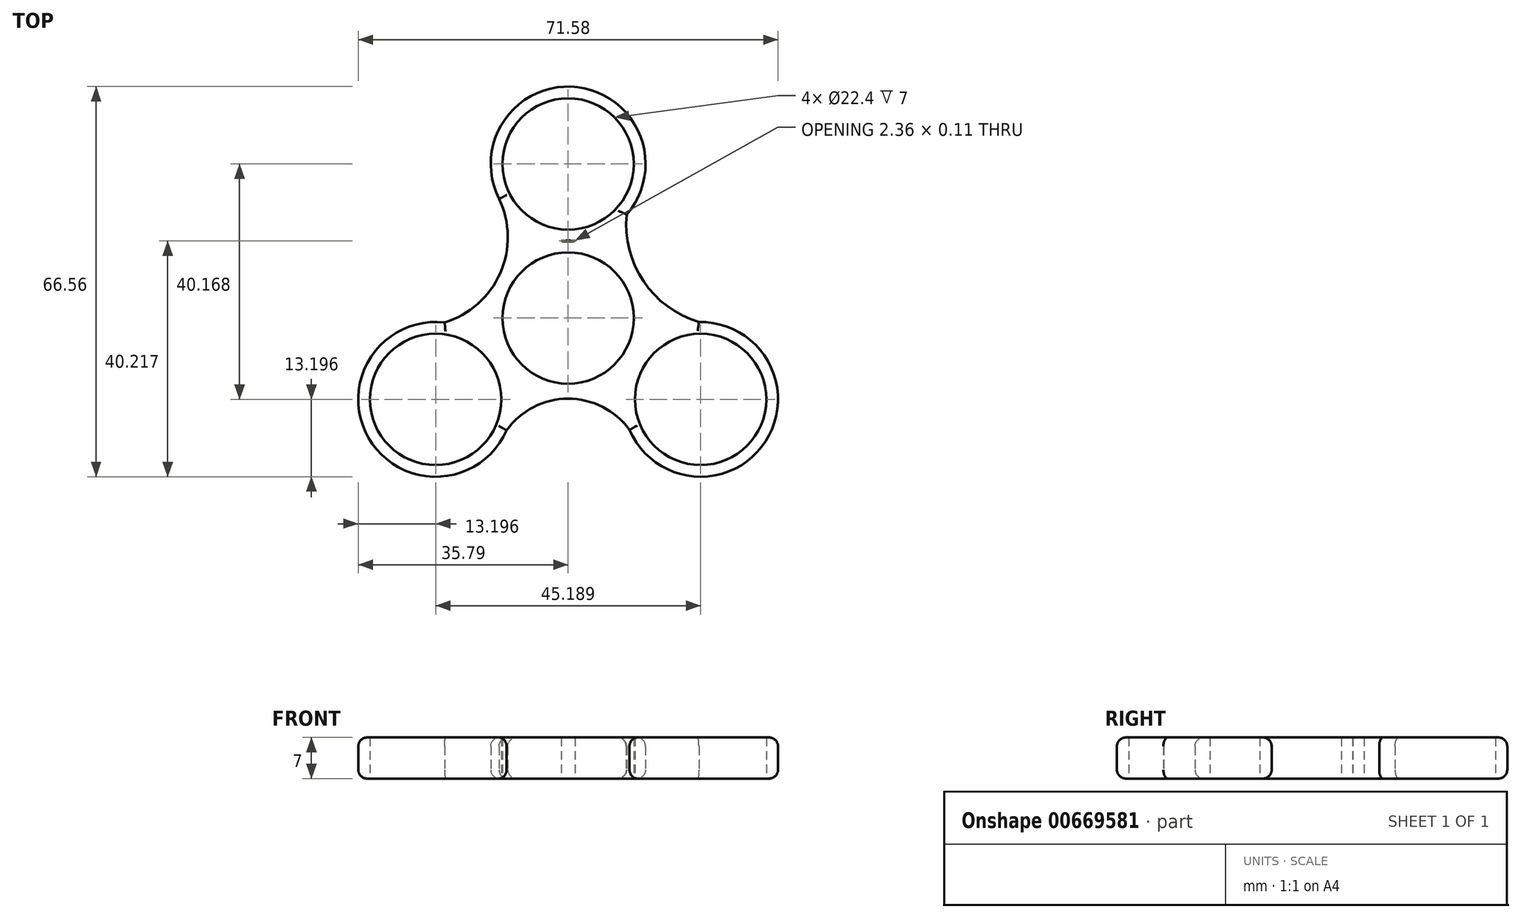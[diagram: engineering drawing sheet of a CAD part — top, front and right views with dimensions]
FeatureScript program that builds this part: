
annotation { "Feature Type Name" : "Feature", "Feature Type Description" : "" }
export const myFeature = defineFeature(function(context is Context, id is Id, definition is map)
    precondition{}
    {
        {
            var Q0;
            Q0=qCreatedBy(makeId("Top.planeOp"),FACE);
            var sketch = newSketch(context, id + "F0", { "sketchPlane" : qUnion([Q0])});
            skCircle(sketch, "E0", {"center": v(0, 0) * mm, "radius": 11.2 * mm});
            skArc(sketch, "E1", {"start": v(1.18, 13.15) * mm, "mid": v(0, 13.2) * mm, "end": v(-1.18, 13.15) * mm});
            skCircle(sketch, "E2", {"center": v(0, 26.3) * mm, "radius": 11.2 * mm});
            skArc(sketch, "E3", {"start": v(9.98, 17.66) * mm, "mid": v(1.62, 39.4) * mm, "end": v(-11.78, 20.34) * mm});
            skCircle(sketch, "E4", {"center": v(-22.6, -13.87) * mm, "radius": 11.2 * mm});
            skArc(sketch, "E5", {"start": v(-21.05, -0.76) * mm, "mid": v(-34.04, -20.45) * mm, "end": v(-10.5, -19.15) * mm});
            skCircle(sketch, "E6", {"center": v(22.6, -13.87) * mm, "radius": 11.2 * mm});
            skArc(sketch, "E7", {"start": v(10.46, -19.08) * mm, "mid": v(33.7, -21.01) * mm, "end": v(22.3, -0.68) * mm});
            skArc(sketch, "E8", {"start": v(9.98, 17.66) * mm, "mid": v(12.85, 6.28) * mm, "end": v(22.3, -0.68) * mm});
            skArc(sketch, "E9", {"start": v(-21.05, -0.76) * mm, "mid": v(-11.58, 7.66) * mm, "end": v(-11.78, 20.34) * mm});
            skArc(sketch, "E10", {"start": v(10.46, -19.08) * mm, "mid": v(-0.03, -13.76) * mm, "end": v(-10.5, -19.15) * mm});
            skArc(sketch, "E11.trimOffspring", {"start": v(-1.18, 13.15) * mm, "mid": v(0, 13.1) * mm, "end": v(1.18, 13.15) * mm});
            skSolve(sketch);
        }
        {
            var Q0;
            Q0 = qSketchRegion(id + "F0", true);
            extrude(context, id + "F1", {"entities" : qUnion([Q0]), "depth" : 7 * mm, "offsetDistance" : 25 * mm});
        }
        {
            var Q0;
            Q0=makeQuery(id+"F1.opExtrude","CAP_EDGE",EDGE,{"disambiguationData":[OSD([sQuery(id+"F0.wireOp",EDGE,"E5")])],"isStart":false});
            var Q1;
            Q1=makeQuery(id+"F1.opExtrude","CAP_EDGE",EDGE,{"disambiguationData":[OSD([sQuery(id+"F0.wireOp",EDGE,"E9")])],"isStart":false});
            var Q2;
            Q2=makeQuery(id+"F1.opExtrude","CAP_EDGE",EDGE,{"disambiguationData":[OSD([sQuery(id+"F0.wireOp",EDGE,"E3")])],"isStart":false});
            var Q3;
            Q3=makeQuery(id+"F1.opExtrude","CAP_EDGE",EDGE,{"disambiguationData":[OSD([sQuery(id+"F0.wireOp",EDGE,"E7")])],"isStart":false});
            var Q4;
            Q4=makeQuery(id+"F1.opExtrude","CAP_EDGE",EDGE,{"disambiguationData":[OSD([sQuery(id+"F0.wireOp",EDGE,"E10")])],"isStart":false});
            var Q5;
            Q5=makeQuery(id+"F1.opExtrude","CAP_EDGE",EDGE,{"disambiguationData":[OSD([sQuery(id+"F0.wireOp",EDGE,"E8")])],"isStart":false});
            fillet(context, id + "F2", {"entities" : qUnion([Q0, Q1, Q2, Q3, Q4, Q5]), "radius" : 1.5 * mm, "tangentPropagation" : true, "allowEdgeOverflow" : false});
        }
        {
            var Q0;
            Q0=makeQuery(id+"F1.opExtrude","CAP_EDGE",EDGE,{"disambiguationData":[OSD([sQuery(id+"F0.wireOp",EDGE,"E5")])],"isStart":true});
            var Q1;
            Q1=makeQuery(id+"F1.opExtrude","CAP_EDGE",EDGE,{"disambiguationData":[OSD([sQuery(id+"F0.wireOp",EDGE,"E10")])],"isStart":true});
            var Q2;
            Q2=makeQuery(id+"F1.opExtrude","CAP_EDGE",EDGE,{"disambiguationData":[OSD([sQuery(id+"F0.wireOp",EDGE,"E9")])],"isStart":true});
            var Q3;
            Q3=makeQuery(id+"F1.opExtrude","CAP_EDGE",EDGE,{"disambiguationData":[OSD([sQuery(id+"F0.wireOp",EDGE,"E7")])],"isStart":true});
            var Q4;
            Q4=makeQuery(id+"F1.opExtrude","CAP_EDGE",EDGE,{"disambiguationData":[OSD([sQuery(id+"F0.wireOp",EDGE,"E8")])],"isStart":true});
            var Q5;
            Q5=makeQuery(id+"F1.opExtrude","CAP_EDGE",EDGE,{"disambiguationData":[OSD([sQuery(id+"F0.wireOp",EDGE,"E3")])],"isStart":true});
            fillet(context, id + "F3", {"entities" : qUnion([Q0, Q1, Q2, Q3, Q4, Q5]), "radius" : 1.5 * mm, "tangentPropagation" : true, "allowEdgeOverflow" : false});
        }
    });
